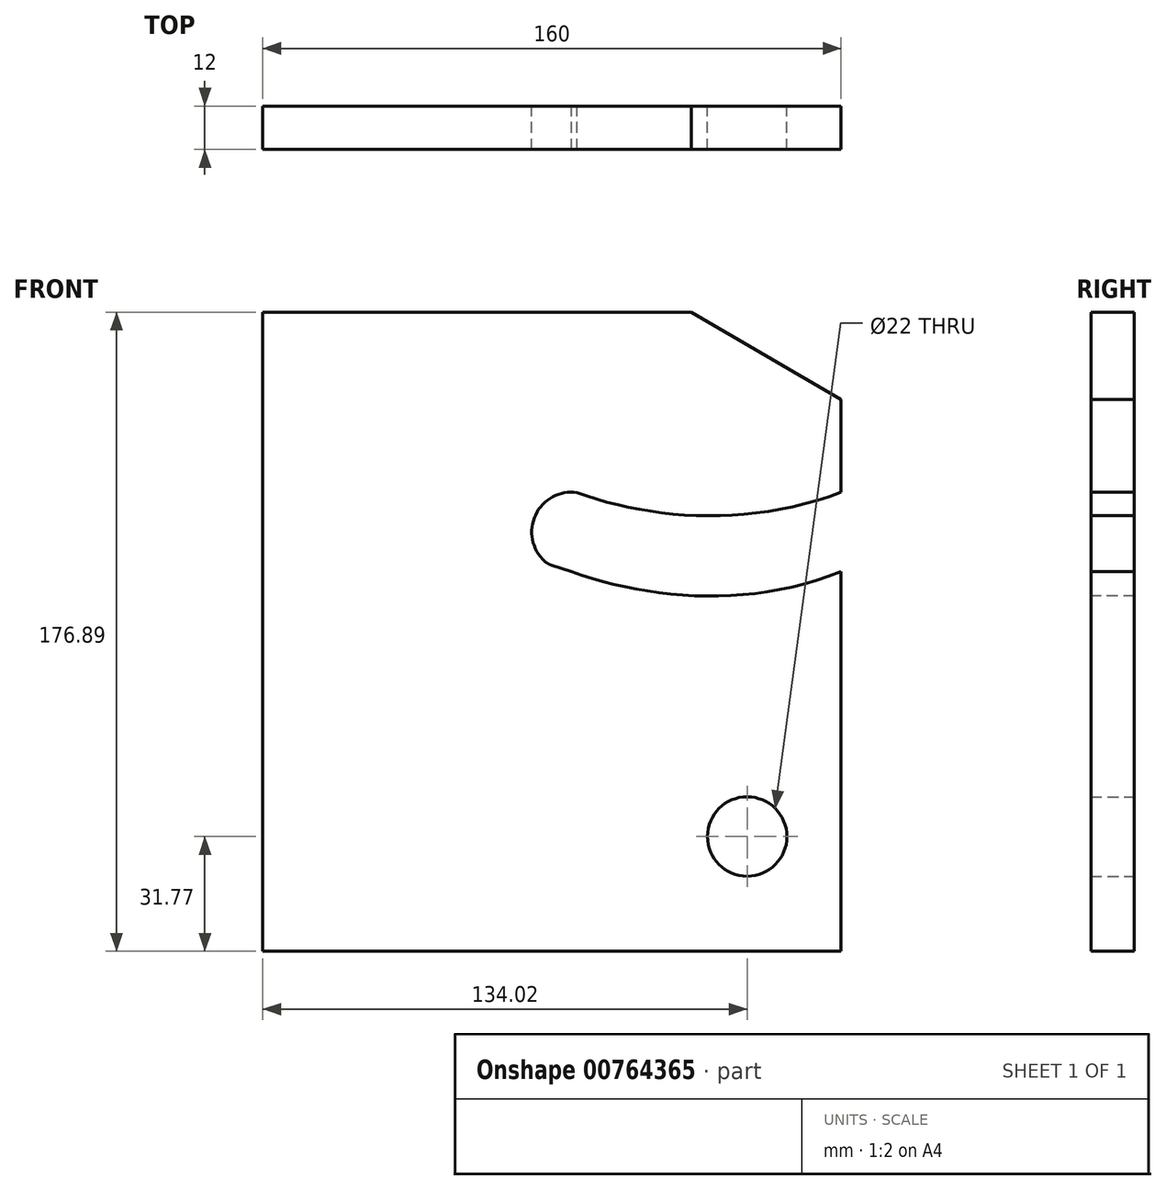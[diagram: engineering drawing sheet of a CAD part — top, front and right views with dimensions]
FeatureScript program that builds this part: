
annotation { "Feature Type Name" : "Feature", "Feature Type Description" : "" }
export const myFeature = defineFeature(function(context is Context, id is Id, definition is map)
    precondition{}
    {
        {
            var Q0;
            Q0=qCreatedBy(makeId("Front.planeOp"),FACE);
            var sketch = newSketch(context, id + "F0", { "sketchPlane" : qUnion([Q0])});
            skLineSegment(sketch, "E0.MirrorCS", {"start": v(-15.44, 102.74) * mm, "end": v(-134.02, 102.74) * mm});
            skLineSegment(sketch, "E1.MirrorCS", {"start": v(25.98, -74.15) * mm, "end": v(-134.02, -74.15) * mm});
            skLineSegment(sketch, "E2.MirrorCS", {"start": v(-134.02, 102.74) * mm, "end": v(-134.02, -74.15) * mm});
            skLineSegment(sketch, "E3", {"start": v(-15.44, 102.74) * mm, "end": v(25.98, 78.6) * mm});
            skLineSegment(sketch, "E4", {"start": v(25.98, 78.6) * mm, "end": v(25.98, 52.88) * mm});
            skCircle(sketch, "E5", {"center": v(0, -42.38) * mm, "radius": 11 * mm});
            skArc(sketch, "E6", {"start": v(-47.07, 52.8) * mm, "mid": v(-58.57, 46.6) * mm, "end": v(-56.02, 33.77) * mm});
            skFitSpline(sketch, "E7", {"points": [v(-48.62, 30.9) * mm, v(25.98, 30.88) * mm], "startDerivative": vector(65.01, -23.02) * mm, "endDerivative": vector(77.94, 30.72) * mm});
            skFitSpline(sketch, "E8", {"points": [v(-48.62, 53.38) * mm, v(25.98, 52.88) * mm], "startDerivative": vector(61.67, -23.83) * mm, "endDerivative": vector(78.34, 29.85) * mm});
            skLineSegment(sketch, "E9.trimOffspring", {"start": v(25.98, 30.88) * mm, "end": v(25.98, -74.15) * mm});
            skLineSegment(sketch, "E10", {"start": v(-48.62, 30.9) * mm, "end": v(-54.2, 32.71) * mm});
            skPoint(sketch, "E11.visualSharp", {"position": v(-55.06, 33) * mm});
            skArc(sketch, "E11.filletArc", {"start": v(-56.02, 33.77) * mm, "mid": v(-55.16, 33.15) * mm, "end": v(-54.2, 32.71) * mm});
            skSolve(sketch);
        }
        {
            var Q0;
            Q0=makeQuery(id+"F0.imprint","IMPRINT",FACE,{"disambiguationData":[TD([[makeQuery(id+"F0.imprint","IMPRINT",EDGE,{"derivedFrom":sQuery(id+"F0.wireOp",EDGE,"E0.MirrorCS")}),1.0]])]});
            extrude(context, id + "F1", {"entities" : qUnion([Q0]), "depth" : 12 * mm, "offsetDistance" : 25 * mm});
        }
    });
